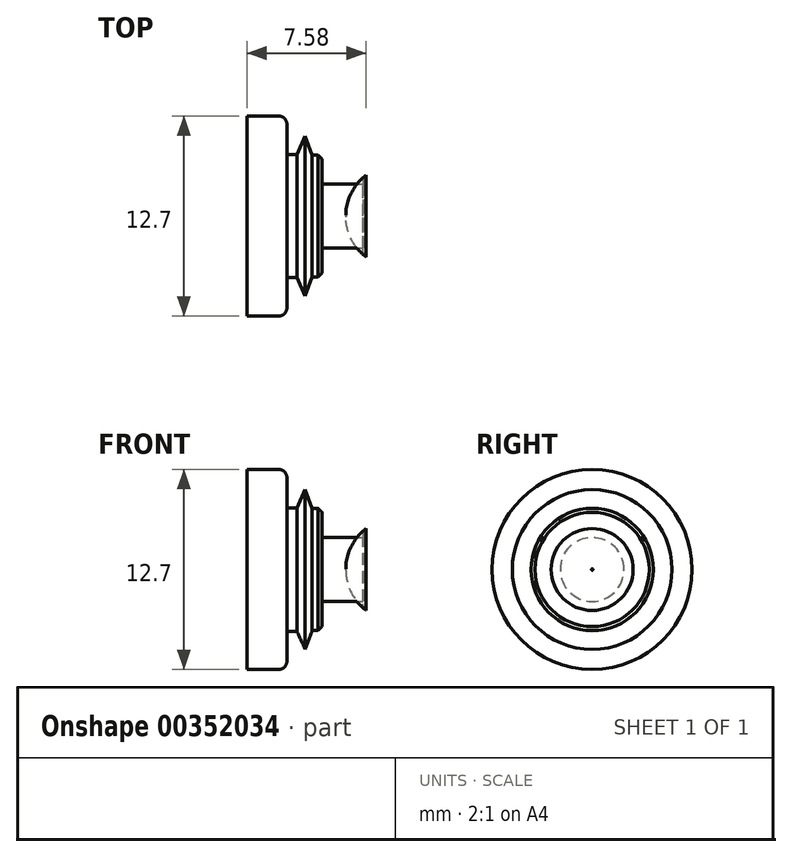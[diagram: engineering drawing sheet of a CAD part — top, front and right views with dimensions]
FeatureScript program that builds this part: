
annotation { "Feature Type Name" : "Feature", "Feature Type Description" : "" }
export const myFeature = defineFeature(function(context is Context, id is Id, definition is map)
    precondition{}
    {
        {
            var Q0;
            Q0=qCreatedBy(makeId("Front.planeOp"),FACE);
            var sketch = newSketch(context, id + "F0", { "sketchPlane" : qUnion([Q0])});
            skLineSegment(sketch, "E0", {"start": v(0, 0) * mm, "end": v(-12.7, 0) * mm});
            skLineSegment(sketch, "E1", {"start": v(-12.7, 0) * mm, "end": v(-12.7, 6.35) * mm});
            skLineSegment(sketch, "E2", {"start": v(-12.7, 6.35) * mm, "end": v(-10.16, 6.35) * mm});
            skLineSegment(sketch, "E3", {"start": v(-10.16, 6.35) * mm, "end": v(-10.16, 3.92) * mm});
            skLineSegment(sketch, "E4", {"start": v(-10.16, 3.92) * mm, "end": v(-9.53, 3.92) * mm});
            skLineSegment(sketch, "E5", {"start": v(-9.53, 3.92) * mm, "end": v(-9, 5.07) * mm});
            skLineSegment(sketch, "E6", {"start": v(-9, 5.07) * mm, "end": v(-8.56, 3.88) * mm});
            skLineSegment(sketch, "E7", {"start": v(-8.56, 3.88) * mm, "end": v(-7.92, 3.88) * mm});
            skLineSegment(sketch, "E8", {"start": v(-7.92, 3.88) * mm, "end": v(-7.92, 2.44) * mm});
            skArc(sketch, "E9", {"start": v(0, 0) * mm, "mid": v(-1.87, 2.94) * mm, "end": v(-5.32, 2.44) * mm});
            skLineSegment(sketch, "E10", {"start": v(-5.32, 2.44) * mm, "end": v(-5.32, 2.03) * mm});
            skLineSegment(sketch, "E11", {"start": v(-5.32, 2.03) * mm, "end": v(-7.92, 2.03) * mm});
            skLineSegment(sketch, "E12", {"start": v(-7.92, 2.44) * mm, "end": v(-7.92, 2.03) * mm});
            skSolve(sketch);
        }
        {
            var Q0;
            Q0=makeQuery(id+"F0.imprint","IMPRINT",FACE,{"disambiguationData":[TD([[makeQuery(id+"F0.imprint","IMPRINT",EDGE,{"derivedFrom":sQuery(id+"F0.wireOp",EDGE,"E0")}),-1.0]])]});
            var Q1;
            Q1=sQuery(id+"F0.wireOp",EDGE,"E0");
            revolve(context, id + "F1", {"entities" : qUnion([Q0]), "axis" : qUnion([Q1]), "revolveType" : RevolveType.FULL});
        }
        {
            var Q0;
            Q0=makeQuery(id+"F1.opRevolve","SWEPT_EDGE",EDGE,{"disambiguationData":[OSD([sQuery(id+"F0.wireOp",EDGE,"E9"),sQuery(id+"F0.wireOp",EDGE,"E10")])]});
            fillet(context, id + "F2", {"entities" : qUnion([Q0]), "radius" : 0.5 * mm, "tangentPropagation" : true, "allowEdgeOverflow" : false});
        }
        {
            var Q0;
            Q0=makeQuery(id+"F1.opRevolve","SWEPT_EDGE",EDGE,{"disambiguationData":[OSD([sQuery(id+"F0.wireOp",EDGE,"E2"),sQuery(id+"F0.wireOp",EDGE,"E3")])]});
            fillet(context, id + "F3", {"entities" : qUnion([Q0]), "radius" : 0.5 * mm, "tangentPropagation" : true, "allowEdgeOverflow" : false});
        }
        {
            var Q0;
            Q0=makeQuery(id+"F1.opRevolve","SWEPT_EDGE",EDGE,{"disambiguationData":[OSD([sQuery(id+"F0.wireOp",EDGE,"E7"),sQuery(id+"F0.wireOp",EDGE,"E8")])]});
            chamfer(context, id + "F4", {"entities" : qUnion([Q0]), "width" : 0.25 * mm, "tangentPropagation" : true});
        }
    });
